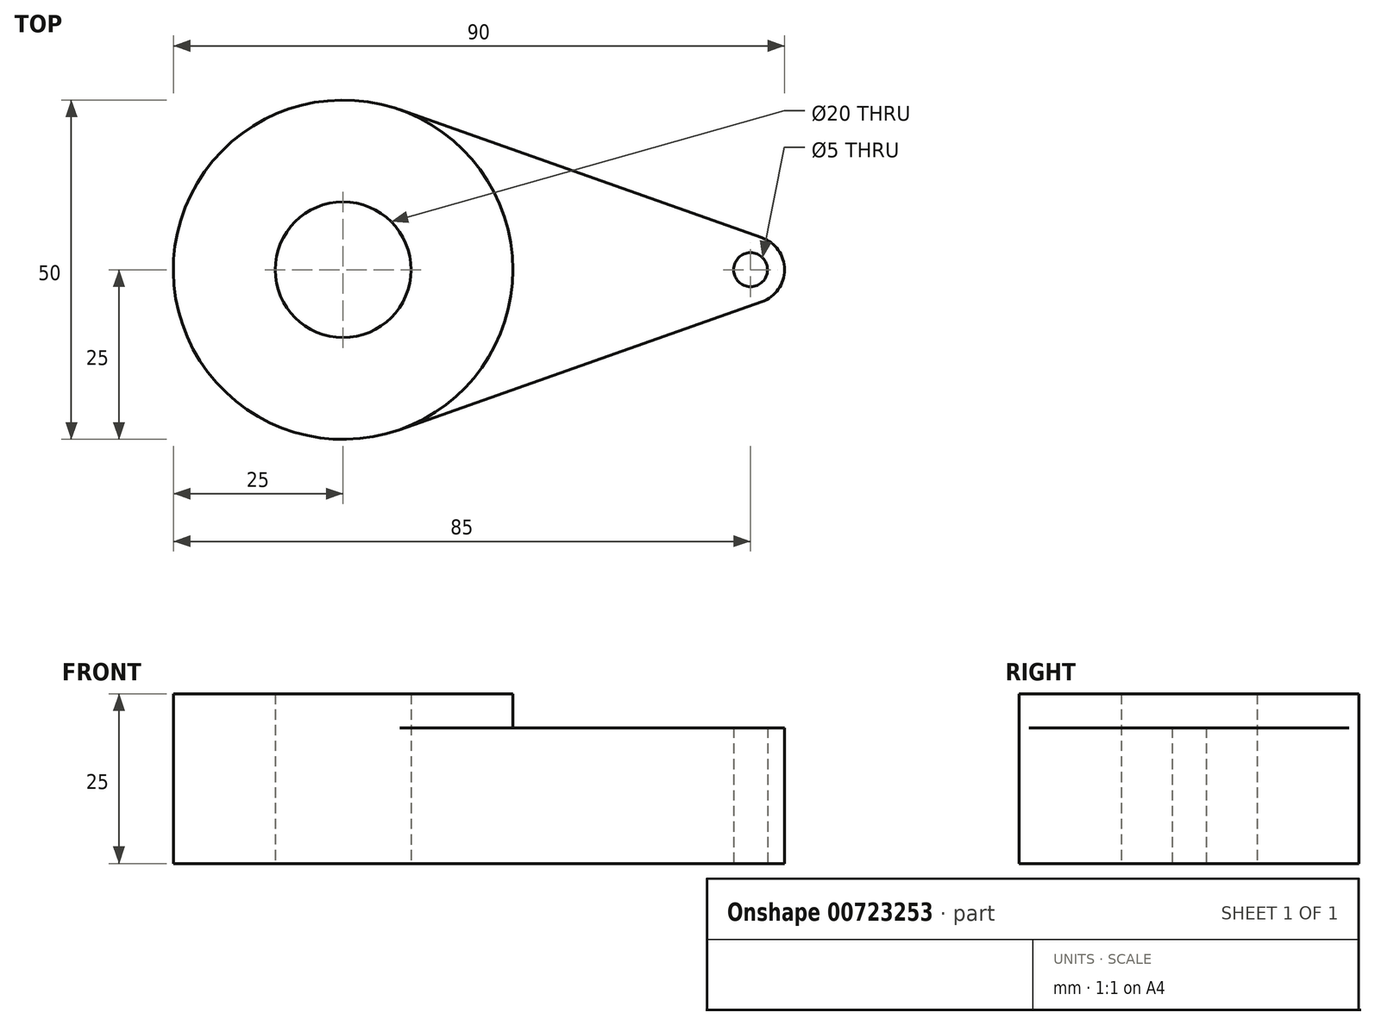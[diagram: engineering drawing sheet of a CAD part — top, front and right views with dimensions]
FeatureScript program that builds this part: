
annotation { "Feature Type Name" : "Feature", "Feature Type Description" : "" }
export const myFeature = defineFeature(function(context is Context, id is Id, definition is map)
    precondition{}
    {
        {
            var Q0;
            Q0=qCreatedBy(makeId("Top.planeOp"),FACE);
            var sketch = newSketch(context, id + "F0", { "sketchPlane" : qUnion([Q0])});
            skCircle(sketch, "E0", {"center": v(0, 0) * mm, "radius": 25 * mm});
            skCircle(sketch, "E1", {"center": v(60, 0) * mm, "radius": 5 * mm});
            skLineSegment(sketch, "E2", {"start": v(8.33, 23.57) * mm, "end": v(61.67, 4.71) * mm});
            skLineSegment(sketch, "E3", {"start": v(8.33, -23.57) * mm, "end": v(61.67, -4.71) * mm});
            skCircle(sketch, "E4", {"center": v(0, 0) * mm, "radius": 10 * mm});
            skCircle(sketch, "E5", {"center": v(60, 0) * mm, "radius": 2.5 * mm});
            skSolve(sketch);
        }
        {
            var Q0;
            Q0 = qSketchRegion(id + "F0", true);
            extrude(context, id + "F1", {"entities" : qUnion([Q0]), "depth" : 20 * mm, "offsetDistance" : 25 * mm});
        }
        {
            var Q0;
            Q0=makeQuery(id+"F0.imprint","IMPRINT",FACE,{"disambiguationData":[TD([[makeQuery(id+"F0.imprint","IMPRINT",EDGE,{"derivedFrom":sQuery(id+"F0.wireOp",EDGE,"E4")}),-1.0]])]});
            extrude(context, id + "F2", {"entities" : qUnion([Q0]), "operationType" : NewBodyOperationType.ADD, "depth" : 25 * mm, "offsetDistance" : 25 * mm});
        }
    });
